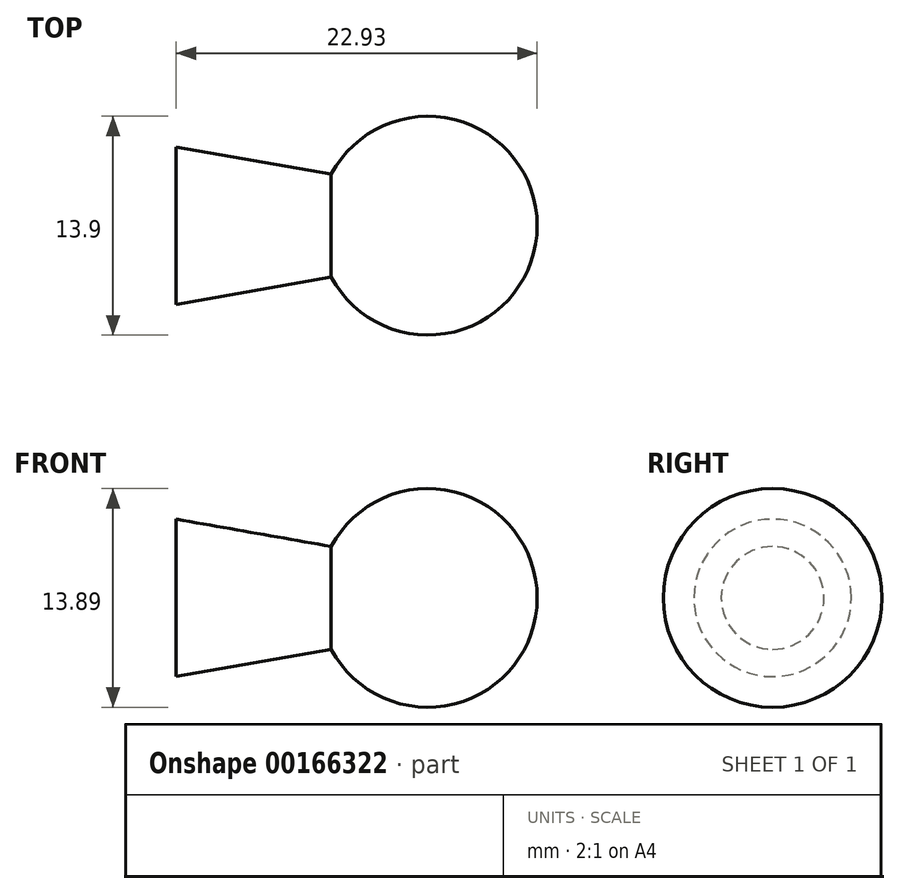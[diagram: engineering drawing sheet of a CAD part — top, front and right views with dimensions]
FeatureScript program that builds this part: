
annotation { "Feature Type Name" : "Feature", "Feature Type Description" : "" }
export const myFeature = defineFeature(function(context is Context, id is Id, definition is map)
    precondition{}
    {
        {
            var Q0;
            Q0=qCreatedBy(makeId("Front.planeOp"),FACE);
            var sketch = newSketch(context, id + "F0", { "sketchPlane" : qUnion([Q0])});
            skLineSegment(sketch, "E0", {"start": v(325.72, -624.16) * mm, "end": v(325.72, -619.16) * mm});
            skLineSegment(sketch, "E1", {"start": v(325.72, -624.16) * mm, "end": v(335.57, -622.43) * mm});
            skLineSegment(sketch, "E2", {"start": v(325.72, -619.16) * mm, "end": v(348.65, -619.16) * mm});
            skArc(sketch, "E3", {"start": v(334.76, -619.16) * mm, "mid": v(341.7, -626.1) * mm, "end": v(348.65, -619.16) * mm});
            skSolve(sketch);
        }
        {
            var Q0;
            Q0 = qSketchRegion(id + "F0", true);
            var Q1;
            Q1=sQuery(id+"F0.wireOp",EDGE,"E2");
            revolve(context, id + "F1", {"entities" : qUnion([Q0]), "axis" : qUnion([Q1]), "revolveType" : RevolveType.FULL});
        }
    });
